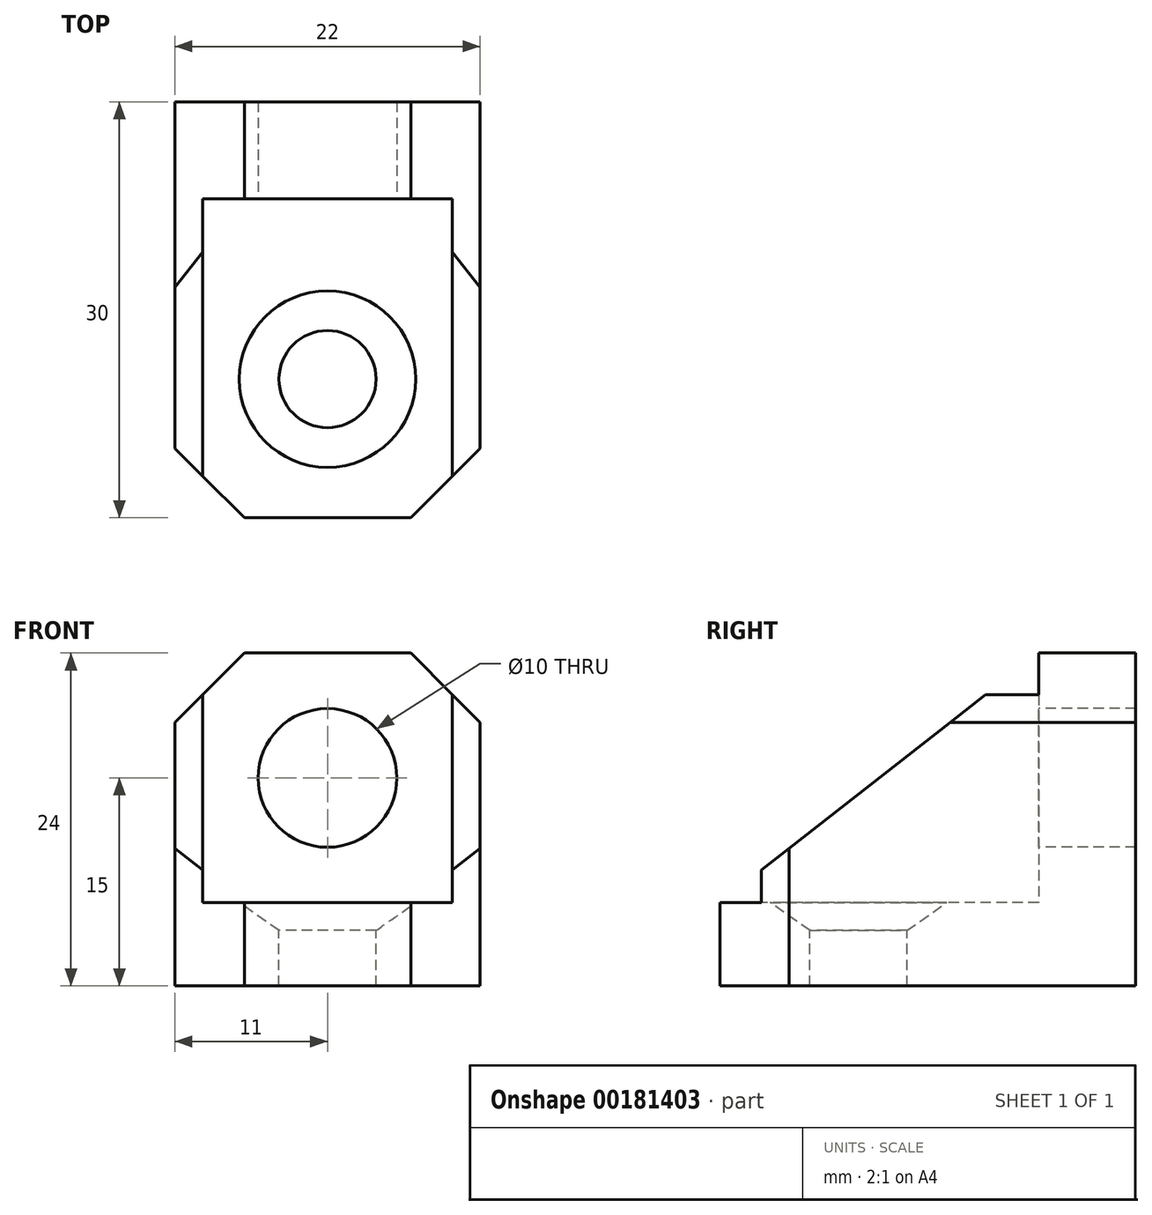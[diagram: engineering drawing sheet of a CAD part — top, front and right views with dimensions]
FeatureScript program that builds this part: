
annotation { "Feature Type Name" : "Feature", "Feature Type Description" : "" }
export const myFeature = defineFeature(function(context is Context, id is Id, definition is map)
    precondition{}
    {
        {
            var Q0;
            Q0=qCreatedBy(makeId("Top.planeOp"),FACE);
            var sketch = newSketch(context, id + "F0", { "sketchPlane" : qUnion([Q0])});
            skLineSegment(sketch, "E0.bottom", {"start": v(11, -15) * mm, "end": v(-11, -15) * mm});
            skLineSegment(sketch, "E0.top", {"start": v(11, 15) * mm, "end": v(-11, 15) * mm});
            skLineSegment(sketch, "E0.left", {"start": v(11, -15) * mm, "end": v(11, 15) * mm});
            skLineSegment(sketch, "E0.right", {"start": v(-11, -15) * mm, "end": v(-11, 15) * mm});
            skPoint(sketch, "E0.middle", {"position": v(0, 0) * mm});
            skLineSegment(sketch, "E1", {"start": v(-11, 8) * mm, "end": v(11, 8) * mm});
            skLineSegment(sketch, "E2", {"start": v(-11, 5) * mm, "end": v(11, 5) * mm, "construction": true});
            skCircle(sketch, "E3", {"center": v(0, -5) * mm, "radius": 3.5 * mm});
            skLineSegment(sketch, "E4", {"start": v(0, 5) * mm, "end": v(0, -15) * mm, "construction": true});
            skLineSegment(sketch, "E5", {"start": v(-9, 8) * mm, "end": v(-9, -15) * mm});
            skLineSegment(sketch, "E6.MirrorCS", {"start": v(9, 8) * mm, "end": v(9, -15) * mm});
            skSolve(sketch);
        }
        {
            var Q0;
            {var subQ3=sQuery(id+"F0.wireOp",EDGE,"E5");Q0=makeQuery(id+"F0.imprint","IMPRINT",FACE,{"disambiguationData":[TD([[makeQuery(id+"F0.imprint","IMPRINT",EDGE,{"derivedFrom":subQ3}),-1.0]])]});}
            var Q1;
            Q1=makeQuery(id+"F0.imprint","IMPRINT",FACE,{"disambiguationData":[TD([[makeQuery(id+"F0.imprint","IMPRINT",EDGE,{"derivedFrom":sQuery(id+"F0.wireOp",EDGE,"E3")}),-1.0]])]});
            var Q2;
            {var subQ3=sQuery(id+"F0.wireOp",EDGE,"E6.MirrorCS");Q2=makeQuery(id+"F0.imprint","IMPRINT",FACE,{"disambiguationData":[TD([[makeQuery(id+"F0.imprint","IMPRINT",EDGE,{"derivedFrom":subQ3}),1.0]])]});}
            var Q3;
            {var subQ4=sQuery(id+"F0.wireOp",EDGE,"E0.top");Q3=makeQuery(id+"F0.imprint","IMPRINT",FACE,{"disambiguationData":[TD([[makeQuery(id+"F0.imprint","IMPRINT",EDGE,{"derivedFrom":subQ4}),1.0]])]});}
            extrude(context, id + "F1", {"entities" : qUnion([Q0, Q1, Q2, Q3]), "oppositeDirection" : true, "depth" : 6 * mm});
        }
        {
            var Q0;
            {var subQ4=sQuery(id+"F0.wireOp",EDGE,"E0.top");Q0=makeQuery(id+"F0.imprint","IMPRINT",FACE,{"disambiguationData":[TD([[makeQuery(id+"F0.imprint","IMPRINT",EDGE,{"derivedFrom":subQ4}),1.0]])]});}
            var Q1;
            {var subQ3=sQuery(id+"F0.wireOp",EDGE,"E5");Q1=makeQuery(id+"F0.imprint","IMPRINT",FACE,{"disambiguationData":[TD([[makeQuery(id+"F0.imprint","IMPRINT",EDGE,{"derivedFrom":subQ3}),-1.0]])]});}
            var Q2;
            {var subQ3=sQuery(id+"F0.wireOp",EDGE,"E6.MirrorCS");Q2=makeQuery(id+"F0.imprint","IMPRINT",FACE,{"disambiguationData":[TD([[makeQuery(id+"F0.imprint","IMPRINT",EDGE,{"derivedFrom":subQ3}),1.0]])]});}
            extrude(context, id + "F2", {"entities" : qUnion([Q0, Q1, Q2]), "operationType" : NewBodyOperationType.ADD, "depth" : 18 * mm});
        }
        {
            var Q0;
            Q0=makeQuery(id+"F2.opExtrude","SWEPT_FACE",FACE,{"disambiguationData":[OSD([sQuery(id+"F0.wireOp",EDGE,"E1")])]});
            var sketch = newSketch(context, id + "F3", { "sketchPlane" : qUnion([Q0])});
            skCircle(sketch, "E7", {"center": v(0, 9) * mm, "radius": 5 * mm});
            skSolve(sketch);
        }
        {
            var Q0;
            Q0=makeQuery(id+"F3.imprint","IMPRINT",FACE,{"disambiguationData":[TD([[makeQuery(id+"F3.imprint","IMPRINT",EDGE,{"derivedFrom":sQuery(id+"F3.wireOp",EDGE,"E7")}),1.0]])]});
            extrude(context, id + "F4", {"entities" : qUnion([Q0]), "operationType" : NewBodyOperationType.REMOVE, "oppositeDirection" : true, "depth" : 25 * mm});
        }
        {
            var Q0;
            {var subQ0=sQuery(id+"F0.wireOp",EDGE,"E0.bottom");Q0=makeQuery(id+"F2.opExtrude","CAP_EDGE",EDGE,{"disambiguationData":[OSD([subQ0]),TDD([makeQuery(id+"F0.imprint","IMPRINT",EDGE,{"disambiguationData":[TD([[makeQuery(id+"F0.imprint","INTERSECT",VERTEX,{"derivedFrom":[subQ0,sQuery(id+"F0.wireOp",EDGE,"E0.right")]}),1.0]])],"derivedFrom":subQ0})])],"isStart":false});}
            var Q1;
            {var subQ0=sQuery(id+"F0.wireOp",EDGE,"E0.bottom");Q1=makeQuery(id+"F2.opExtrude","CAP_EDGE",EDGE,{"disambiguationData":[OSD([subQ0]),TDD([makeQuery(id+"F0.imprint","IMPRINT",EDGE,{"disambiguationData":[TD([[makeQuery(id+"F0.imprint","INTERSECT",VERTEX,{"derivedFrom":[subQ0,sQuery(id+"F0.wireOp",EDGE,"E0.left")]}),-1.0]])],"derivedFrom":subQ0})])],"isStart":false});}
            chamfer(context, id + "F5", {"entities" : qUnion([Q0, Q1]), "chamferType" : ChamferType.TWO_OFFSETS, "width1" : 18 * mm, "oppositeDirection" : false, "width2" : 23 * mm, "tangentPropagation" : true});
        }
        {
            var Q0;
            {var subQ0=sQuery(id+"F0.wireOp",EDGE,"E0.left");var subQ1=sQuery(id+"F0.wireOp",EDGE,"E0.bottom");Q0=makeQuery(id+"F2.boolean.opBoolean","MERGE",EDGE,{"derivedFrom":[makeQuery(id+"F1.opExtrude","SWEPT_EDGE",EDGE,{"disambiguationData":[OSD([subQ1,subQ0])]}),makeQuery(id+"F2.opExtrude","SWEPT_EDGE",EDGE,{"disambiguationData":[OSD([subQ1,subQ0])]})]});}
            var Q1;
            {var subQ0=sQuery(id+"F0.wireOp",EDGE,"E0.right");var subQ1=sQuery(id+"F0.wireOp",EDGE,"E0.bottom");Q1=makeQuery(id+"F2.boolean.opBoolean","MERGE",EDGE,{"derivedFrom":[makeQuery(id+"F1.opExtrude","SWEPT_EDGE",EDGE,{"disambiguationData":[OSD([subQ1,subQ0])]}),makeQuery(id+"F2.opExtrude","SWEPT_EDGE",EDGE,{"disambiguationData":[OSD([subQ1,subQ0])]})]});}
            var Q2;
            Q2=makeQuery(id+"F2.opExtrude","CAP_EDGE",EDGE,{"disambiguationData":[OSD([sQuery(id+"F0.wireOp",EDGE,"E0.left")])],"isStart":false});
            var Q3;
            Q3=makeQuery(id+"F2.opExtrude","CAP_EDGE",EDGE,{"disambiguationData":[OSD([sQuery(id+"F0.wireOp",EDGE,"E0.right")])],"isStart":false});
            chamfer(context, id + "F6", {"entities" : qUnion([Q0, Q1, Q2, Q3]), "width" : 5 * mm, "tangentPropagation" : true});
        }
        {
            var Q0;
            Q0=makeQuery(id+"F1.opExtrude","CAP_EDGE",EDGE,{"disambiguationData":[OSD([sQuery(id+"F0.wireOp",EDGE,"E3")])],"isStart":true});
            chamfer(context, id + "F7", {"entities" : qUnion([Q0]), "chamferType" : ChamferType.OFFSET_ANGLE, "width" : 2 * mm, "oppositeDirection" : false, "angle" : 55 * degree, "tangentPropagation" : true});
        }
    });
